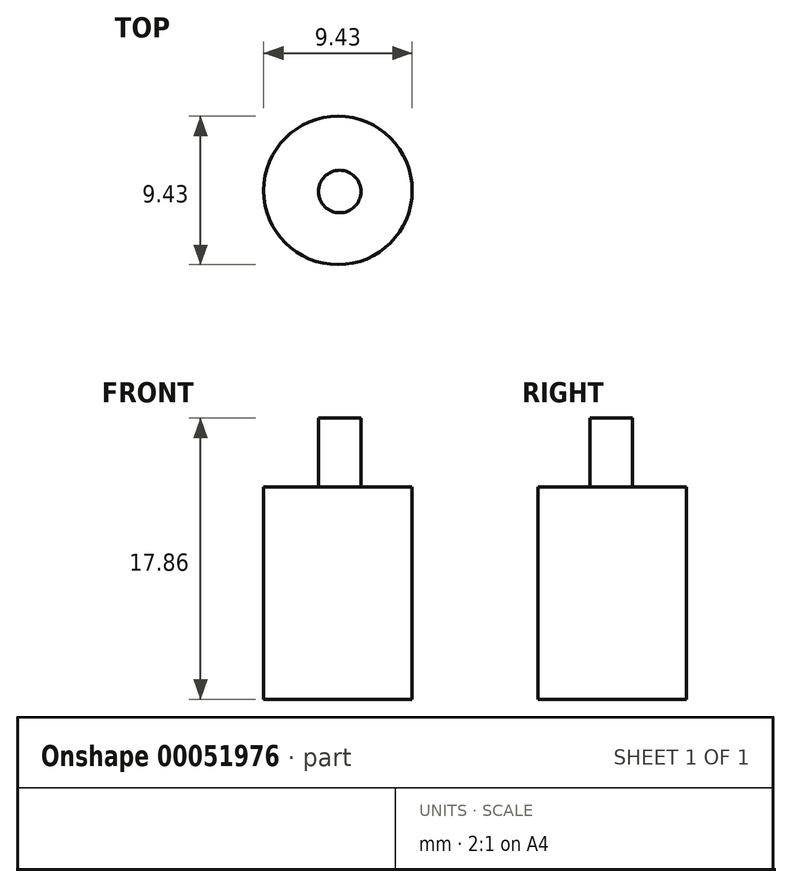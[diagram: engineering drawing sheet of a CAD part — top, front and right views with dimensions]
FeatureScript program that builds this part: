
annotation { "Feature Type Name" : "Feature", "Feature Type Description" : "" }
export const myFeature = defineFeature(function(context is Context, id is Id, definition is map)
    precondition{}
    {
        {
            var Q0;
            Q0=qCreatedBy(makeId("Top.planeOp"),FACE);
            var sketch = newSketch(context, id + "F0", { "sketchPlane" : qUnion([Q0])});
            skCircle(sketch, "E0", {"center": v(-41.43, 24.8) * mm, "radius": 4.71 * mm});
            skSolve(sketch);
        }
        {
            var Q0;
            Q0 = qSketchRegion(id + "F0", true);
            extrude(context, id + "F1", {"entities" : qUnion([Q0]), "depth" : 13.48 * mm});
        }
        {
            var Q0;
            Q0=qCreatedBy(makeId("Top.planeOp"),FACE);
            var sketch = newSketch(context, id + "F2", { "sketchPlane" : qUnion([Q0])});
            skCircle(sketch, "E1", {"center": v(-41.32, 24.73) * mm, "radius": 1.35 * mm});
            skSolve(sketch);
        }
        {
            var Q0;
            Q0 = qSketchRegion(id + "F2", true);
            extrude(context, id + "F3", {"entities" : qUnion([Q0]), "operationType" : NewBodyOperationType.ADD, "depth" : 17.86 * mm});
        }
    });
